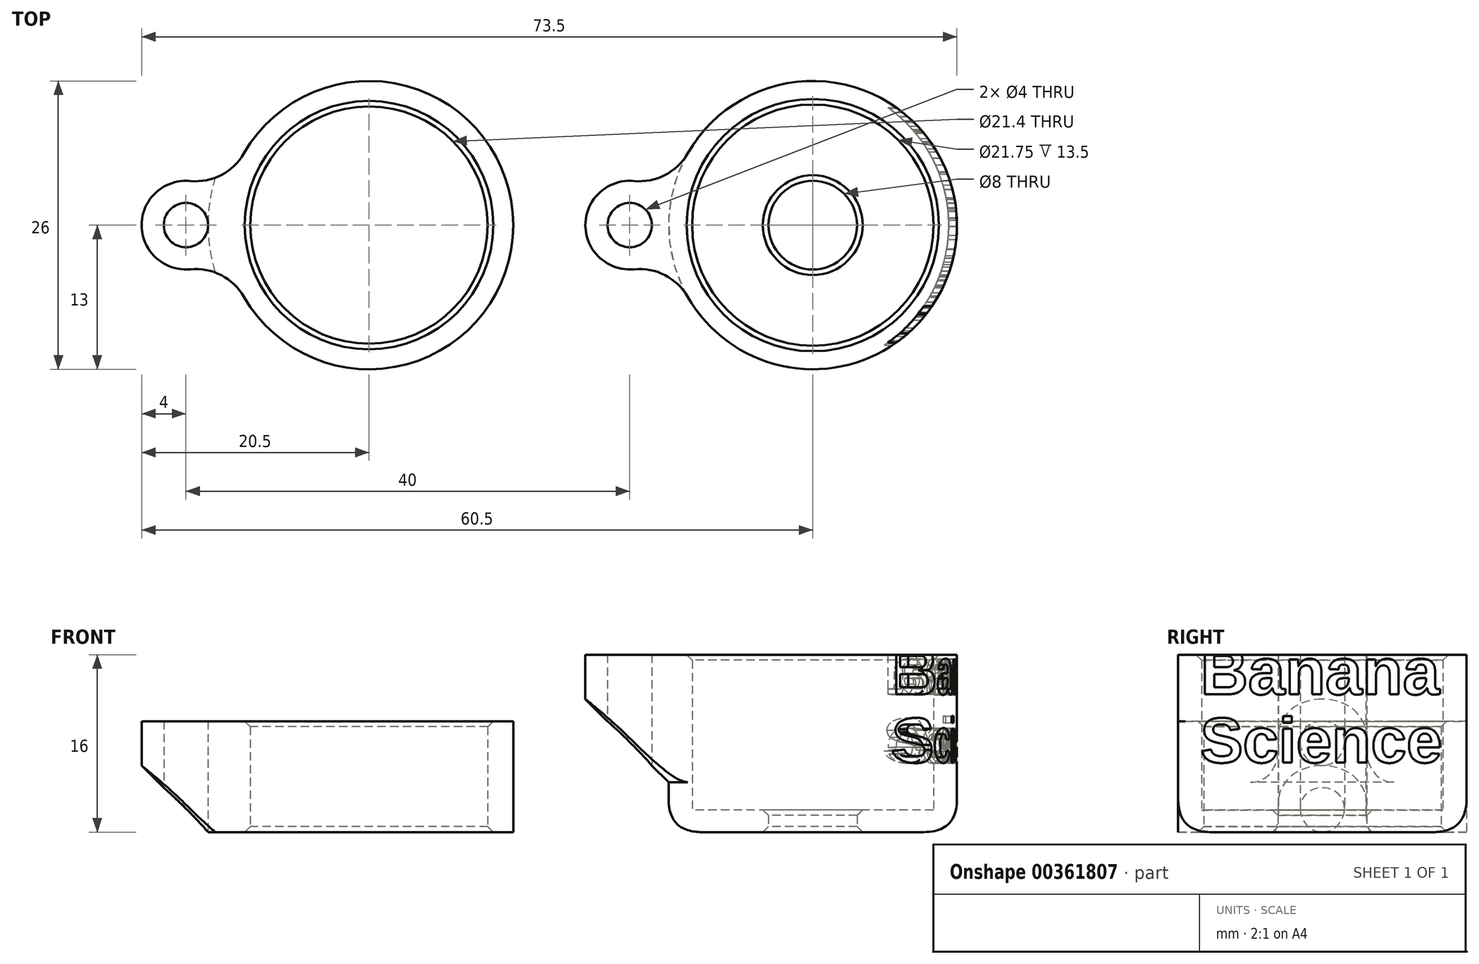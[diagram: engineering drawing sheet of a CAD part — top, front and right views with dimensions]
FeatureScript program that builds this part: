
annotation { "Feature Type Name" : "Feature", "Feature Type Description" : "" }
export const myFeature = defineFeature(function(context is Context, id is Id, definition is map)
    precondition{}
    {
        {
            var Q0;
            Q0=qCreatedBy(makeId("Top.planeOp"),FACE);
            var sketch = newSketch(context, id + "F0", { "sketchPlane" : qUnion([Q0])});
            skCircle(sketch, "E0", {"center": v(0, 0) * mm, "radius": 10.88 * mm});
            skCircle(sketch, "E1", {"center": v(0, 0) * mm, "radius": 13 * mm});
            skCircle(sketch, "E2", {"center": v(-16.5, 0) * mm, "radius": 4 * mm});
            skCircle(sketch, "E3", {"center": v(-16.5, 0) * mm, "radius": 2 * mm});
            skCircle(sketch, "E4", {"center": v(0, 0) * mm, "radius": 4 * mm});
            skSolve(sketch);
        }
        {
            var Q0;
            Q0=makeQuery(id+"F0.imprint","IMPRINT",FACE,{"disambiguationData":[TD([[makeQuery(id+"F0.imprint","IMPRINT",EDGE,{"derivedFrom":sQuery(id+"F0.wireOp",EDGE,"E0")}),-1.0]])]});
            var Q1;
            {var subQ0=sQuery(id+"F0.wireOp",EDGE,"E2");var subQ1=sQuery(id+"F0.wireOp",EDGE,"E1");var subQ2=makeQuery(id+"F0.imprint","INTERSECT",VERTEX,{"disambiguationData":[OD(0.0)],"derivedFrom":[subQ1,subQ0]});Q1=makeQuery(id+"F0.imprint","IMPRINT",FACE,{"disambiguationData":[TD([[makeQuery(id+"F0.imprint","IMPRINT",EDGE,{"disambiguationData":[TD([[subQ2,1.0]])],"derivedFrom":subQ1}),1.0]])]});}
            extrude(context, id + "F1", {"entities" : qUnion([Q0, Q1]), "depth" : 16 * mm, "offsetDistance" : 25 * mm});
        }
        {
            var Q0;
            Q0=makeQuery(id+"F0.imprint","IMPRINT",FACE,{"disambiguationData":[TD([[makeQuery(id+"F0.imprint","IMPRINT",EDGE,{"derivedFrom":sQuery(id+"F0.wireOp",EDGE,"E0")}),1.0]])]});
            extrude(context, id + "F2", {"entities" : qUnion([Q0]), "operationType" : NewBodyOperationType.ADD, "depth" : 2 * mm, "offsetDistance" : 25 * mm});
        }
        {
            var Q0;
            Q0=qCreatedBy(makeId("Top.planeOp"),FACE);
            var sketch = newSketch(context, id + "F3", { "sketchPlane" : qUnion([Q0])});
            skCircle(sketch, "E5", {"center": v(-40, 0) * mm, "radius": 13 * mm});
            skCircle(sketch, "E6", {"center": v(-40, 0) * mm, "radius": 10.7 * mm});
            skCircle(sketch, "E7", {"center": v(-56.5, 0) * mm, "radius": 4 * mm});
            skCircle(sketch, "E8", {"center": v(-56.5, 0) * mm, "radius": 2 * mm});
            skSolve(sketch);
        }
        {
            var Q0;
            Q0=makeQuery(id+"F3.imprint","IMPRINT",FACE,{"disambiguationData":[TD([[makeQuery(id+"F3.imprint","IMPRINT",EDGE,{"derivedFrom":sQuery(id+"F3.wireOp",EDGE,"E6")}),-1.0]])]});
            var Q1;
            {var subQ0=sQuery(id+"F3.wireOp",EDGE,"E7");var subQ1=sQuery(id+"F3.wireOp",EDGE,"E5");var subQ2=makeQuery(id+"F3.imprint","INTERSECT",VERTEX,{"disambiguationData":[OD(0.0)],"derivedFrom":[subQ1,subQ0]});Q1=makeQuery(id+"F3.imprint","IMPRINT",FACE,{"disambiguationData":[TD([[makeQuery(id+"F3.imprint","IMPRINT",EDGE,{"disambiguationData":[TD([[subQ2,1.0]])],"derivedFrom":subQ1}),1.0]])]});}
            extrude(context, id + "F4", {"entities" : qUnion([Q0, Q1]), "depth" : 10 * mm, "offsetDistance" : 25 * mm});
        }
        {
            var Q0;
            Q0=makeQuery(id+"F1.opExtrude","CAP_EDGE",EDGE,{"disambiguationData":[OSD([sQuery(id+"F0.wireOp",EDGE,"E1")])],"isStart":true});
            var Q1;
            Q1=makeQuery(id+"F2.opExtrude","CAP_EDGE",EDGE,{"disambiguationData":[OSD([sQuery(id+"F0.wireOp",EDGE,"E0")])],"isStart":false});
            fillet(context, id + "F5", {"entities" : qUnion([Q0, Q1]), "radius" : 3 * mm, "tangentPropagation" : true, "rho" : 0.5, "crossSection" : FilletCrossSection.CONIC, "allowEdgeOverflow" : false});
        }
        {
            var Q0;
            Q0=makeQuery(id+"F1.opExtrude","CAP_EDGE",EDGE,{"disambiguationData":[OSD([sQuery(id+"F0.wireOp",EDGE,"E0")])],"isStart":false});
            var Q1;
            Q1=makeQuery(id+"F2.opExtrude","CAP_EDGE",EDGE,{"disambiguationData":[OSD([sQuery(id+"F0.wireOp",EDGE,"6ru0MfPZ-ubaX-B0dC-GUrv-7Vsd5N7kwgG7")])],"isStart":true});
            var Q2;
            Q2=makeQuery(id+"F2.opExtrude","CAP_EDGE",EDGE,{"disambiguationData":[OSD([sQuery(id+"F0.wireOp",EDGE,"6ru0MfPZ-ubaX-B0dC-GUrv-7Vsd5N7kwgG7")])],"isStart":false});
            var Q3;
            Q3=makeQuery(id+"F2.opExtrude","CAP_EDGE",EDGE,{"disambiguationData":[OSD([sQuery(id+"F0.wireOp",EDGE,"E4")])],"isStart":true});
            var Q4;
            Q4=makeQuery(id+"F2.opExtrude","CAP_EDGE",EDGE,{"disambiguationData":[OSD([sQuery(id+"F0.wireOp",EDGE,"E4")])],"isStart":false});
            var Q5;
            Q5=makeQuery(id+"F4.opExtrude","CAP_EDGE",EDGE,{"disambiguationData":[OSD([sQuery(id+"F3.wireOp",EDGE,"E6")])],"isStart":false});
            var Q6;
            Q6=makeQuery(id+"F4.opExtrude","CAP_EDGE",EDGE,{"disambiguationData":[OSD([sQuery(id+"F3.wireOp",EDGE,"E6")])],"isStart":true});
            chamfer(context, id + "F6", {"entities" : qUnion([Q0, Q1, Q2, Q3, Q4, Q5, Q6]), "width" : .5 * mm, "tangentPropagation" : true});
        }
        {
            var Q0;
            Q0=qCreatedBy(makeId("Right.planeOp"),FACE);
            cPlane(context, id + "F7", {"entities" : qUnion([Q0]), "cplaneType" : CPlaneType.OFFSET, "offset" : (26 / 2) * mm, "width" : 150 * mm, "height" : 150 * mm});
        }
        {
            var Q0;
            Q0=qCreatedBy(id+"F7.planeOp",FACE);
            var sketch = newSketch(context, id + "F8", { "sketchPlane" : qUnion([Q0])});
            skText(sketch, "E9", { "text": "Banana\n", "fontName": "Arimo-Bold.ttf"});
            skText(sketch, "E10", { "text": "Science", "fontName": "Arimo-Bold.ttf"});
            skLineSegment(sketch, "E11", {"start": v(0, 14.72) * mm, "end": v(0, 16) * mm, "construction": true});
            skLineSegment(sketch, "E12", {"start": v(0, 4.28) * mm, "end": v(0, 3) * mm, "construction": true});
            const initialGuessF8  = {"E9": [-0.011, 0.01243, 1, 0, 0.0043], "E10": [-0.011, 0.00628, 1, 0, 0.00415]};
            skSetInitialGuess(sketch, initialGuessF8);
            skSolve(sketch);
        }
        {
            var Q0;
            Q0=makeQuery(id+"F8.imprint","IMPRINT",FACE,{"disambiguationData":[TD([[makeQuery(id+"F8.imprint","IMPRINT",EDGE,{"derivedFrom":sQuery(id+"F8.wireOp",EDGE,"E9.sketch_text.stroke-0")}),-1.0]])]});
            var Q1;
            Q1=makeQuery(id+"F8.imprint","IMPRINT",FACE,{"disambiguationData":[TD([[makeQuery(id+"F8.imprint","IMPRINT",EDGE,{"derivedFrom":sQuery(id+"F8.wireOp",EDGE,"E9.sketch_text.stroke-24")}),-1.0]])]});
            var Q2;
            Q2=makeQuery(id+"F8.imprint","IMPRINT",FACE,{"disambiguationData":[TD([[makeQuery(id+"F8.imprint","IMPRINT",EDGE,{"derivedFrom":sQuery(id+"F8.wireOp",EDGE,"E9.sketch_text.stroke-62")}),-1.0]])]});
            var Q3;
            Q3=makeQuery(id+"F8.imprint","IMPRINT",FACE,{"disambiguationData":[TD([[makeQuery(id+"F8.imprint","IMPRINT",EDGE,{"derivedFrom":sQuery(id+"F8.wireOp",EDGE,"E9.sketch_text.stroke-81")}),-1.0]])]});
            var Q4;
            Q4=makeQuery(id+"F8.imprint","IMPRINT",FACE,{"disambiguationData":[TD([[makeQuery(id+"F8.imprint","IMPRINT",EDGE,{"derivedFrom":sQuery(id+"F8.wireOp",EDGE,"E10.sketch_text.stroke-0")}),-1.0]])]});
            var Q5;
            Q5=makeQuery(id+"F8.imprint","IMPRINT",FACE,{"disambiguationData":[TD([[makeQuery(id+"F8.imprint","IMPRINT",EDGE,{"derivedFrom":sQuery(id+"F8.wireOp",EDGE,"E10.sketch_text.stroke-31")}),-1.0]])]});
            var Q6;
            Q6=makeQuery(id+"F8.imprint","IMPRINT",FACE,{"disambiguationData":[TD([[makeQuery(id+"F8.imprint","IMPRINT",EDGE,{"derivedFrom":sQuery(id+"F8.wireOp",EDGE,"E10.sketch_text.stroke-52")}),-1.0]])]});
            var Q7;
            Q7=makeQuery(id+"F8.imprint","IMPRINT",FACE,{"disambiguationData":[TD([[makeQuery(id+"F8.imprint","IMPRINT",EDGE,{"derivedFrom":sQuery(id+"F8.wireOp",EDGE,"E10.sketch_text.stroke-48")}),-1.0]])]});
            var Q8;
            Q8=makeQuery(id+"F8.imprint","IMPRINT",FACE,{"disambiguationData":[TD([[makeQuery(id+"F8.imprint","IMPRINT",EDGE,{"derivedFrom":sQuery(id+"F8.wireOp",EDGE,"E10.sketch_text.stroke-56")}),-1.0]])]});
            var Q9;
            Q9=makeQuery(id+"F8.imprint","IMPRINT",FACE,{"disambiguationData":[TD([[makeQuery(id+"F8.imprint","IMPRINT",EDGE,{"derivedFrom":sQuery(id+"F8.wireOp",EDGE,"E10.sketch_text.stroke-74")}),-1.0]])]});
            var Q10;
            Q10=makeQuery(id+"F8.imprint","IMPRINT",FACE,{"disambiguationData":[TD([[makeQuery(id+"F8.imprint","IMPRINT",EDGE,{"derivedFrom":sQuery(id+"F8.wireOp",EDGE,"E10.sketch_text.stroke-93")}),-1.0]])]});
            var Q11;
            Q11=makeQuery(id+"F8.imprint","IMPRINT",FACE,{"disambiguationData":[TD([[makeQuery(id+"F8.imprint","IMPRINT",EDGE,{"derivedFrom":sQuery(id+"F8.wireOp",EDGE,"E10.sketch_text.stroke-110")}),-1.0]])]});
            var Q12;
            Q12=makeQuery(id+"F8.imprint","IMPRINT",FACE,{"disambiguationData":[TD([[makeQuery(id+"F8.imprint","IMPRINT",EDGE,{"derivedFrom":sQuery(id+"F8.wireOp",EDGE,"E9.sketch_text.stroke-119")}),-1.0]])]});
            var Q13;
            Q13=makeQuery(id+"F8.imprint","IMPRINT",FACE,{"disambiguationData":[TD([[makeQuery(id+"F8.imprint","IMPRINT",EDGE,{"derivedFrom":sQuery(id+"F8.wireOp",EDGE,"E9.sketch_text.stroke-138")}),-1.0]])]});
            var Q14;
            Q14=makeQuery(id+"F1.opExtrude","SWEPT_FACE",FACE,{"disambiguationData":[OSD([sQuery(id+"F0.wireOp",EDGE,"E1")])]});
            extrude(context, id + "F9", {"entities" : qUnion([Q0, Q1, Q2, Q3, Q4, Q5, Q6, Q7, Q8, Q9, Q10, Q11, Q12, Q13]), "operationType" : NewBodyOperationType.REMOVE, "endBound" : BoundingType.UP_TO_SURFACE, "oppositeDirection" : true, "depth" : 25 * mm, "endBoundEntityFace" : qUnion([Q14]), "hasOffset" : true, "offsetDistance" : .75 * mm, "offsetOppositeDirection" : true});
        }
        {
            var Q0;
            Q0=makeQuery(id+"F3.imprint","IMPRINT",FACE,{"disambiguationData":[TD([[makeQuery(id+"F3.imprint","IMPRINT",EDGE,{"derivedFrom":sQuery(id+"F3.wireOp",EDGE,"E8")}),-1.0]])]});
            var Q1;
            {var subQ0=sQuery(id+"F3.wireOp",EDGE,"E7");var subQ1=sQuery(id+"F3.wireOp",EDGE,"E5");var subQ2=makeQuery(id+"F3.imprint","INTERSECT",VERTEX,{"disambiguationData":[OD(0.0)],"derivedFrom":[subQ1,subQ0]});Q1=makeQuery(id+"F3.imprint","IMPRINT",FACE,{"disambiguationData":[TD([[makeQuery(id+"F3.imprint","IMPRINT",EDGE,{"disambiguationData":[TD([[subQ2,1.0]])],"derivedFrom":subQ1}),1.0]])]});}
            extrude(context, id + "F10", {"entities" : qUnion([Q0, Q1]), "operationType" : NewBodyOperationType.ADD, "depth" : 10 * mm, "offsetDistance" : 25 * mm, "hasSecondDirection" : true, "secondDirectionOppositeDirection" : false, "secondDirectionDepth" : 6 * mm});
        }
        {
            var Q0;
            Q0=makeQuery(id+"F0.imprint","IMPRINT",FACE,{"disambiguationData":[TD([[makeQuery(id+"F0.imprint","IMPRINT",EDGE,{"derivedFrom":sQuery(id+"F0.wireOp",EDGE,"E3")}),-1.0]])]});
            var Q1;
            {var subQ0=sQuery(id+"F0.wireOp",EDGE,"E2");var subQ1=sQuery(id+"F0.wireOp",EDGE,"E1");var subQ2=makeQuery(id+"F0.imprint","INTERSECT",VERTEX,{"disambiguationData":[OD(0.0)],"derivedFrom":[subQ1,subQ0]});Q1=makeQuery(id+"F0.imprint","IMPRINT",FACE,{"disambiguationData":[TD([[makeQuery(id+"F0.imprint","IMPRINT",EDGE,{"disambiguationData":[TD([[subQ2,1.0]])],"derivedFrom":subQ1}),1.0]])]});}
            extrude(context, id + "F11", {"entities" : qUnion([Q0, Q1]), "operationType" : NewBodyOperationType.ADD, "depth" : 16 * mm, "offsetDistance" : 25 * mm, "hasSecondDirection" : true, "secondDirectionOppositeDirection" : false, "secondDirectionDepth" : 12 * mm});
        }
        {
            var Q0;
            {var subQ0=sQuery(id+"F0.wireOp",EDGE,"E1");Q0=makeQuery(id+"F11.boolean.opBoolean","INTERSECT",EDGE,{"derivedFrom":[makeQuery(id+"F9.boolean.opBoolean","SPLIT",FACE,{"disambiguationData":[TD([makeQuery(id+"F5.opFillet","BLEND_FACE",FACE,{"disambiguationData":[OSD([subQ0])]})])],"derivedFrom":makeQuery(id+"F1.opExtrude","SWEPT_FACE",FACE,{"disambiguationData":[OSD([subQ0])]})}),makeQuery(id+"F11.opExtrude","CAP_FACE",FACE,{"disambiguationData":[OSD([sQuery(id+"F0.wireOp",EDGE,"E2"),sQuery(id+"F0.wireOp",EDGE,"E3")])],"isStart":true})]});}
            var Q1;
            Q1=makeQuery(id+"F10.boolean.opBoolean","INTERSECT",EDGE,{"derivedFrom":[makeQuery(id+"F4.opExtrude","SWEPT_FACE",FACE,{"disambiguationData":[OSD([sQuery(id+"F3.wireOp",EDGE,"E5")])]}),makeQuery(id+"F10.opExtrude","CAP_FACE",FACE,{"disambiguationData":[OSD([sQuery(id+"F3.wireOp",EDGE,"E7"),sQuery(id+"F3.wireOp",EDGE,"E8")])],"isStart":true})]});
            chamfer(context, id + "F12", {"entities" : qUnion([Q0, Q1]), "width" : 7.5 * mm, "tangentPropagation" : true});
        }
        {
            var Q0;
            {var subQ0=sQuery(id+"F0.wireOp",EDGE,"E1");Q0=makeQuery(id+"F11.boolean.opBoolean","INTERSECT",EDGE,{"disambiguationData":[OD(0.0)],"derivedFrom":[makeQuery(id+"F9.boolean.opBoolean","SPLIT",FACE,{"disambiguationData":[TD([makeQuery(id+"F5.opFillet","BLEND_FACE",FACE,{"disambiguationData":[OSD([subQ0])]})])],"derivedFrom":makeQuery(id+"F1.opExtrude","SWEPT_FACE",FACE,{"disambiguationData":[OSD([subQ0])]})}),makeQuery(id+"F11.opExtrude","SWEPT_FACE",FACE,{"disambiguationData":[OSD([sQuery(id+"F0.wireOp",EDGE,"E2")])]})]});}
            var Q1;
            {var subQ0=sQuery(id+"F0.wireOp",EDGE,"E1");Q1=makeQuery(id+"F11.boolean.opBoolean","INTERSECT",EDGE,{"disambiguationData":[OD(1.0)],"derivedFrom":[makeQuery(id+"F9.boolean.opBoolean","SPLIT",FACE,{"disambiguationData":[TD([makeQuery(id+"F5.opFillet","BLEND_FACE",FACE,{"disambiguationData":[OSD([subQ0])]})])],"derivedFrom":makeQuery(id+"F1.opExtrude","SWEPT_FACE",FACE,{"disambiguationData":[OSD([subQ0])]})}),makeQuery(id+"F11.opExtrude","SWEPT_FACE",FACE,{"disambiguationData":[OSD([sQuery(id+"F0.wireOp",EDGE,"E2")])]})]});}
            var Q2;
            {var subQ0=sQuery(id+"F3.wireOp",EDGE,"E7");var subQ1=sQuery(id+"F3.wireOp",EDGE,"E5");Q2=makeQuery(id+"F4.opExtrude","SWEPT_EDGE",EDGE,{"disambiguationData":[OSD([subQ1,subQ0]),TDD([makeQuery(id+"F3.imprint","INTERSECT",VERTEX,{"disambiguationData":[OD(0.0)],"derivedFrom":[subQ1,subQ0]})])]});}
            var Q3;
            {var subQ0=sQuery(id+"F3.wireOp",EDGE,"E7");var subQ1=sQuery(id+"F3.wireOp",EDGE,"E5");Q3=makeQuery(id+"F4.opExtrude","SWEPT_EDGE",EDGE,{"disambiguationData":[OSD([subQ1,subQ0]),TDD([makeQuery(id+"F3.imprint","INTERSECT",VERTEX,{"disambiguationData":[OD(1.0)],"derivedFrom":[subQ1,subQ0]})])]});}
            var Q4;
            Q4=makeQuery(id+"F10.boolean.opBoolean","INTERSECT",EDGE,{"disambiguationData":[OD(1.0)],"derivedFrom":[makeQuery(id+"F4.opExtrude","SWEPT_FACE",FACE,{"disambiguationData":[OSD([sQuery(id+"F3.wireOp",EDGE,"E5")])]}),makeQuery(id+"F10.opExtrude","SWEPT_FACE",FACE,{"disambiguationData":[OSD([sQuery(id+"F3.wireOp",EDGE,"E7")])]})]});
            var Q5;
            Q5=makeQuery(id+"F10.boolean.opBoolean","INTERSECT",EDGE,{"disambiguationData":[OD(0.0)],"derivedFrom":[makeQuery(id+"F4.opExtrude","SWEPT_FACE",FACE,{"disambiguationData":[OSD([sQuery(id+"F3.wireOp",EDGE,"E5")])]}),makeQuery(id+"F10.opExtrude","SWEPT_FACE",FACE,{"disambiguationData":[OSD([sQuery(id+"F3.wireOp",EDGE,"E7")])]})]});
            fillet(context, id + "F13", {"entities" : qUnion([Q0, Q1, Q2, Q3, Q4, Q5]), "radius" : 5 * mm, "tangentPropagation" : true, "allowEdgeOverflow" : false});
        }
    });
